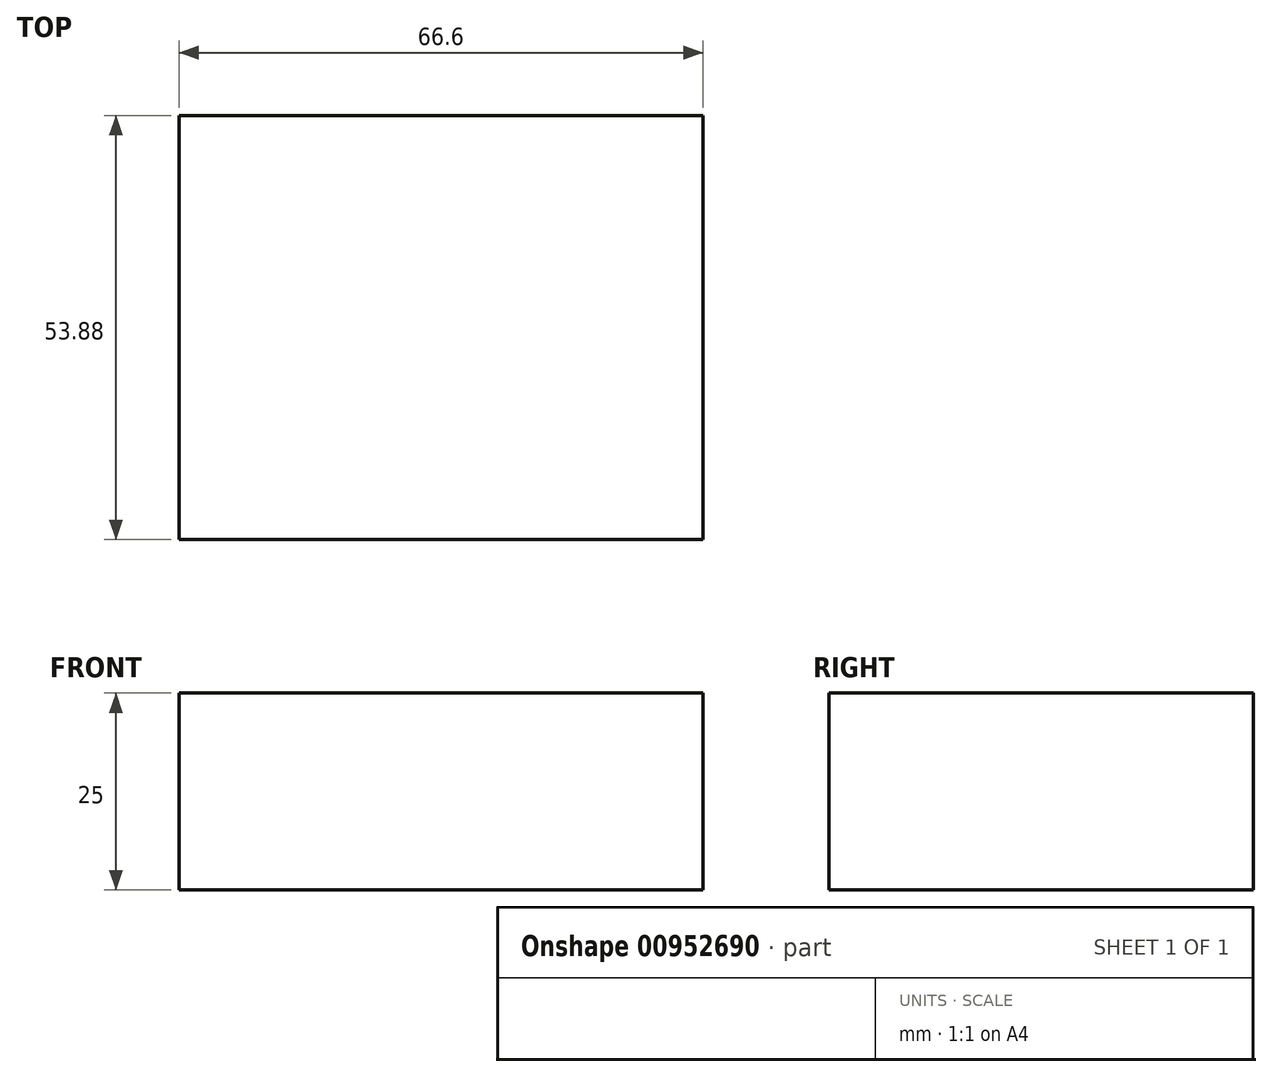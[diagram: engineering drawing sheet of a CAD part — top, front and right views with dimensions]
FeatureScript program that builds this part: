
annotation { "Feature Type Name" : "Feature", "Feature Type Description" : "" }
export const myFeature = defineFeature(function(context is Context, id is Id, definition is map)
    precondition{}
    {
        {
            var Q0;
            Q0=qCreatedBy(makeId("Top.planeOp"),FACE);
            var sketch = newSketch(context, id + "F0", { "sketchPlane" : qUnion([Q0])});
            skLineSegment(sketch, "E0.bottom", {"start": v(-43.98, -34.2) * mm, "end": v(22.62, -34.2) * mm});
            skLineSegment(sketch, "E0.top", {"start": v(-43.98, 19.67) * mm, "end": v(22.62, 19.67) * mm});
            skLineSegment(sketch, "E0.left", {"start": v(-43.98, -34.2) * mm, "end": v(-43.98, 19.67) * mm});
            skLineSegment(sketch, "E0.right", {"start": v(22.62, -34.2) * mm, "end": v(22.62, 19.67) * mm});
            skSolve(sketch);
        }
        {
            var Q0;
            Q0 = qSketchRegion(id + "F0", true);
            extrude(context, id + "F1", {"entities" : qUnion([Q0]), "depth" : 25 * mm, "offsetDistance" : 25 * mm});
        }
    });
